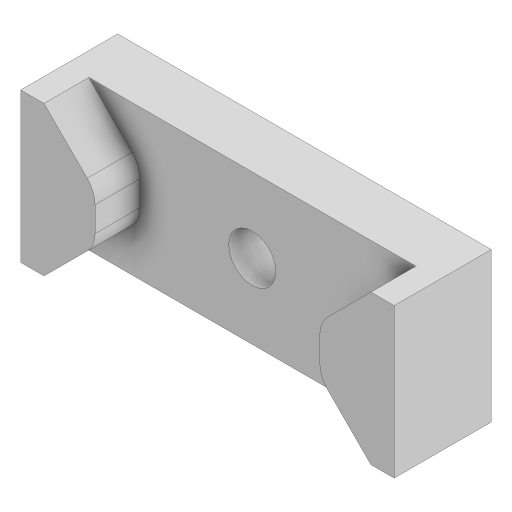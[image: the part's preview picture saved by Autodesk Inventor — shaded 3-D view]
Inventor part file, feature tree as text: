
AUTODESK INVENTOR PART (.ipt)
format: ipt  version: 2023 (Build 270158000, 158)  size: 149,504 bytes
history: native  units: mm
features: extrude x2, sketch x2, projected_geometry x1
ambient origin geometry x8: Origin, YZ Plane, XZ Plane, XY Plane, X Axis, Y Axis, Z Axis, Center Point
bodies: Solid1 (feature_tree)
feature tree (5):
  extrude  "Extrusion1"  Depth=25.0mm
  extrude  "Extrusion2"  Depth=3.5mm TaperAngle=0.0deg
  sketch  "Sketch1"  dims[d0=3.15mm d1=25.0mm]
  sketch  "Sketch3"  dims[d2=10.0mm d3=3.5mm d4=0.0mm d5=0.2mm d6=0.2mm d7=0.2mm d8=0.2mm d9=0.2mm d10=0.2mm d11=0.2mm d12=0.2mm d13=0.2mm d14=3.0mm d15=0.0mm d16=0.5mm d17=0.872665mm]
  projected_geometry  "Projected Loop1"
